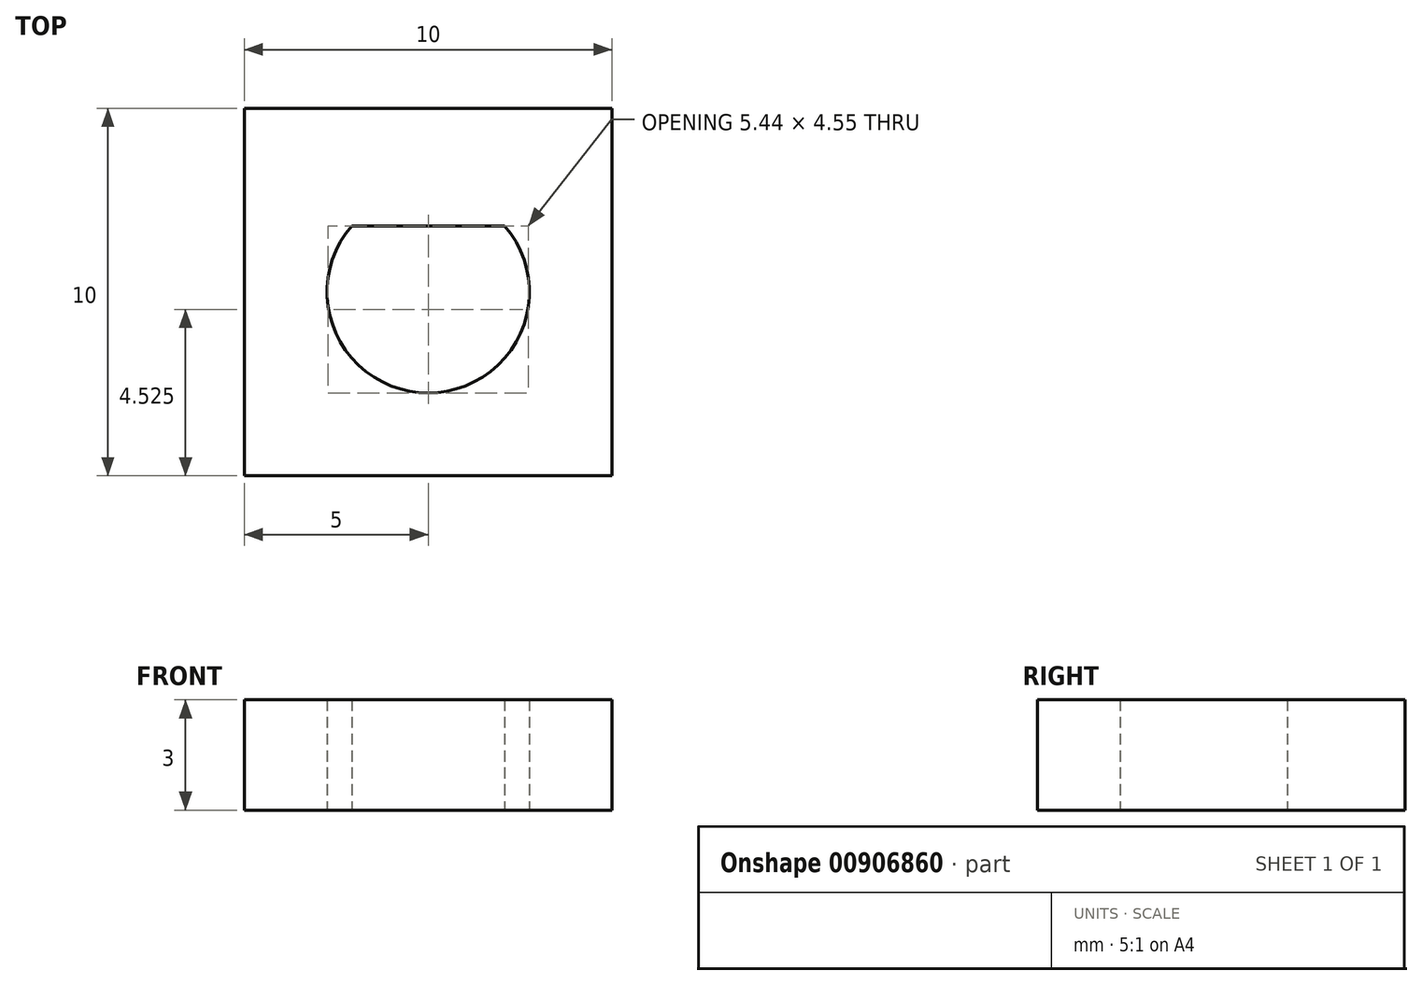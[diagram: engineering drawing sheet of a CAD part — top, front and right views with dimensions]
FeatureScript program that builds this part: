
annotation { "Feature Type Name" : "Feature", "Feature Type Description" : "" }
export const myFeature = defineFeature(function(context is Context, id is Id, definition is map)
    precondition{}
    {
        {
            var Q0;
            Q0=qCreatedBy(makeId("Top.planeOp"),FACE);
            var sketch = newSketch(context, id + "F0", { "sketchPlane" : qUnion([Q0])});
            skArc(sketch, "E0", {"start": v(-2.08, 1.8) * mm, "mid": v(0, -2.75) * mm, "end": v(2.08, 1.8) * mm});
            skLineSegment(sketch, "E1.bottom", {"start": v(5, 5) * mm, "end": v(-5, 5) * mm});
            skLineSegment(sketch, "E1.top", {"start": v(5, -5) * mm, "end": v(-5, -5) * mm});
            skLineSegment(sketch, "E1.left", {"start": v(5, 5) * mm, "end": v(5, -5) * mm});
            skLineSegment(sketch, "E1.right", {"start": v(-5, 5) * mm, "end": v(-5, -5) * mm});
            skLineSegment(sketch, "E2", {"start": v(-2.08, 1.8) * mm, "end": v(2.08, 1.8) * mm});
            skSolve(sketch);
        }
        {
            var Q0;
            Q0 = qSketchRegion(id + "F0", true);
            extrude(context, id + "F1", {"entities" : qUnion([Q0]), "depth" : 3 * mm, "offsetDistance" : 25 * mm});
        }
    });
